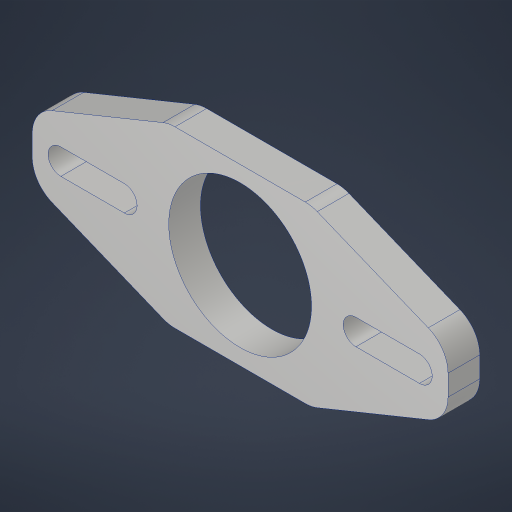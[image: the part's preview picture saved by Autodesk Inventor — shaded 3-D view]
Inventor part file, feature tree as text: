
AUTODESK INVENTOR PART (.ipt)
format: ipt  version: 2023.4 (Build 274418000, 418)  size: 231,936 bytes
history: native  units: in
note: dims shown in document units (in); Inventor stores cm internally (conversion verified against a paired STEP export)
features: extrude x1, fillet x1, plane x1, sketch x1
ambient origin geometry x8: Origin, YZ Plane, XZ Plane, XY Plane, X Axis, Y Axis, Z Axis, Center Point
bodies: Solid1 (feature_tree)
feature tree (4):
  extrude  "Extrusion1"  Depth=0.25in TaperAngle=0.0deg
  fillet  "Fillet1"  Radius=1.125in
  plane  "Work Plane1"
  sketch  "Sketch1"  dims[d0=1.125in d1=0.25in d2=0.0in d3=1.125in d4=0.125in d5=0.6875in d6=0.6875in d7=0.5in d8=0.5in d9=0.25in d10=0.201in d11=1.163in d12=0.375in d13=1.074in d16=4.297in d19=1.432in d20=4.201in d21=2.0in d22=1.163in d23=0.125in d24=0.2255in d25=0.2255in d26=0.5in d27=0.25in]
